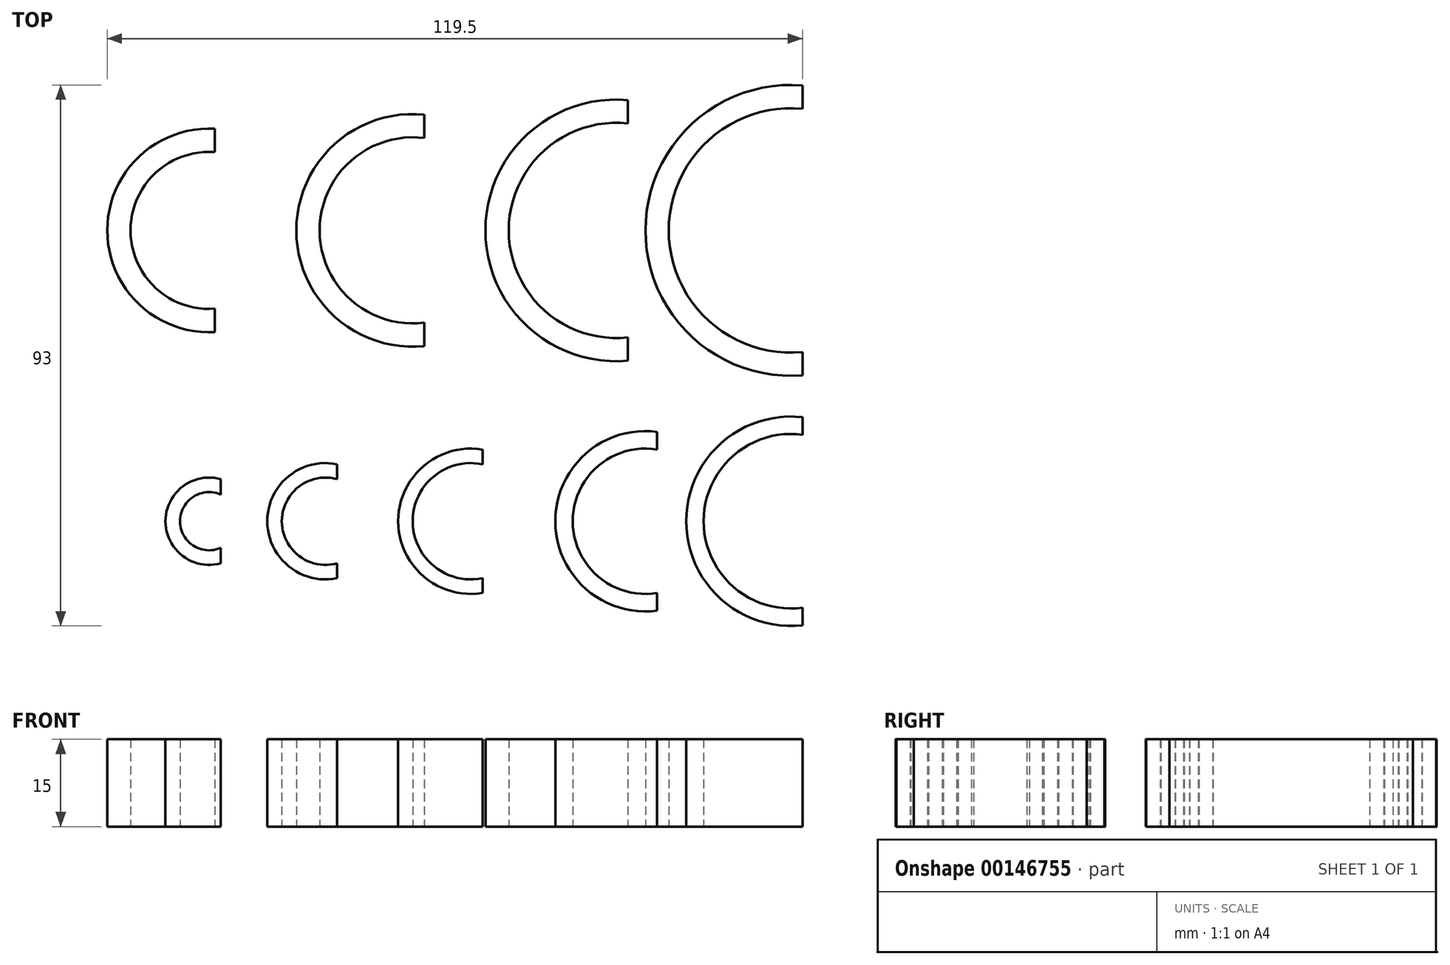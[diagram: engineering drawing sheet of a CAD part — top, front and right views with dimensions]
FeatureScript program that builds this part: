
annotation { "Feature Type Name" : "Feature", "Feature Type Description" : "" }
export const myFeature = defineFeature(function(context is Context, id is Id, definition is map)
    precondition{}
    {
        {
            var Q0;
            Q0=qCreatedBy(makeId("Top.planeOp"),FACE);
            var sketch = newSketch(context, id + "F0", { "sketchPlane" : qUnion([Q0])});
            skArc(sketch, "E0", {"start": v(2, 4.58) * mm, "mid": v(-5, 0) * mm, "end": v(2, -4.58) * mm});
            skLineSegment(sketch, "E1", {"start": v(0, 100) * mm, "end": v(0, 0) * mm, "construction": true});
            skLineSegment(sketch, "E2", {"start": v(0, 0) * mm, "end": v(100, 0) * mm, "construction": true});
            skArc(sketch, "E3", {"start": v(22, 7.23) * mm, "mid": v(12.5, 0) * mm, "end": v(22, -7.23) * mm});
            skArc(sketch, "E4", {"start": v(47, 9.8) * mm, "mid": v(35, 0) * mm, "end": v(47, -9.8) * mm});
            skArc(sketch, "E5", {"start": v(77, 12.34) * mm, "mid": v(62.5, 0) * mm, "end": v(77, -12.34) * mm});
            skArc(sketch, "E6", {"start": v(2, 7.23) * mm, "mid": v(-7.5, 0) * mm, "end": v(2, -7.23) * mm});
            skArc(sketch, "E7", {"start": v(22, 9.8) * mm, "mid": v(10, 0) * mm, "end": v(22, -9.8) * mm});
            skArc(sketch, "E8", {"start": v(47, 12.34) * mm, "mid": v(32.5, 0) * mm, "end": v(47, -12.34) * mm});
            skArc(sketch, "E9", {"start": v(77, 15.37) * mm, "mid": v(59.5, 0) * mm, "end": v(77, -15.37) * mm});
            skLineSegment(sketch, "E10", {"start": v(2, 7.23) * mm, "end": v(2, 4.58) * mm});
            skLineSegment(sketch, "E11", {"start": v(22, 9.8) * mm, "end": v(22, 7.23) * mm});
            skLineSegment(sketch, "E12", {"start": v(47, 12.34) * mm, "end": v(47, 9.8) * mm});
            skLineSegment(sketch, "E13", {"start": v(77, 15.37) * mm, "end": v(77, 12.34) * mm});
            skLineSegment(sketch, "E14.trimOffspring", {"start": v(77, -12.34) * mm, "end": v(77, -15.37) * mm});
            skLineSegment(sketch, "E15.trimOffspring", {"start": v(47, -9.8) * mm, "end": v(47, -12.34) * mm});
            skLineSegment(sketch, "E16.trimOffspring", {"start": v(22, -7.23) * mm, "end": v(22, -9.8) * mm});
            skLineSegment(sketch, "E17.trimOffspring", {"start": v(2, -4.58) * mm, "end": v(2, -7.23) * mm});
            skLineSegment(sketch, "E18", {"start": v(0, 50) * mm, "end": v(100, 50) * mm, "construction": true});
            skArc(sketch, "E19", {"start": v(1, 67.47) * mm, "mid": v(-17.5, 50) * mm, "end": v(1, 32.53) * mm});
            skArc(sketch, "E20", {"start": v(1, 63.46) * mm, "mid": v(-13.5, 50) * mm, "end": v(1, 36.54) * mm});
            skArc(sketch, "E21", {"start": v(37, 69.9) * mm, "mid": v(15, 50) * mm, "end": v(37, 30.1) * mm});
            skArc(sketch, "E22", {"start": v(37, 65.87) * mm, "mid": v(19, 50) * mm, "end": v(37, 34.13) * mm});
            skArc(sketch, "E23", {"start": v(72, 72.41) * mm, "mid": v(47.5, 50) * mm, "end": v(72, 27.59) * mm});
            skArc(sketch, "E24", {"start": v(72, 68.4) * mm, "mid": v(51.5, 50) * mm, "end": v(72, 31.6) * mm});
            skArc(sketch, "E25", {"start": v(102, 17.89) * mm, "mid": v(82, 0) * mm, "end": v(102, -17.89) * mm});
            skArc(sketch, "E26", {"start": v(102, 14.87) * mm, "mid": v(85, 0) * mm, "end": v(102, -14.87) * mm});
            skLineSegment(sketch, "E27", {"start": v(102, 17.89) * mm, "end": v(102, 14.87) * mm});
            skLineSegment(sketch, "E28.trimOffspring", {"start": v(102, -14.87) * mm, "end": v(102, -17.89) * mm});
            skPoint(sketch, "E29.center.orphan", {"position": v(50, 50) * mm});
            skLineSegment(sketch, "E30", {"start": v(1, 67.47) * mm, "end": v(1, 63.46) * mm});
            skLineSegment(sketch, "E31", {"start": v(37, 69.9) * mm, "end": v(37, 65.87) * mm});
            skLineSegment(sketch, "E32", {"start": v(72, 72.41) * mm, "end": v(72, 68.4) * mm});
            skLineSegment(sketch, "E33.trimOffspring", {"start": v(1, 36.54) * mm, "end": v(1, 32.53) * mm});
            skLineSegment(sketch, "E34.trimOffspring", {"start": v(37, 34.13) * mm, "end": v(37, 30.1) * mm});
            skLineSegment(sketch, "E35.trimOffspring", {"start": v(72, 31.6) * mm, "end": v(72, 27.59) * mm});
            skArc(sketch, "E36", {"start": v(102, 74.92) * mm, "mid": v(75, 50) * mm, "end": v(102, 25.08) * mm});
            skArc(sketch, "E37", {"start": v(102, 70.9) * mm, "mid": v(79, 50) * mm, "end": v(102, 29.1) * mm});
            skLineSegment(sketch, "E38", {"start": v(102, 74.92) * mm, "end": v(102, 70.9) * mm});
            skLineSegment(sketch, "E39.trimOffspring", {"start": v(102, 29.1) * mm, "end": v(102, 25.08) * mm});
            skSolve(sketch);
        }
        {
            var Q0;
            Q0 = qSketchRegion(id + "F0", true);
            extrude(context, id + "F1", {"entities" : qUnion([Q0]), "depth" : 15 * mm});
        }
    });
